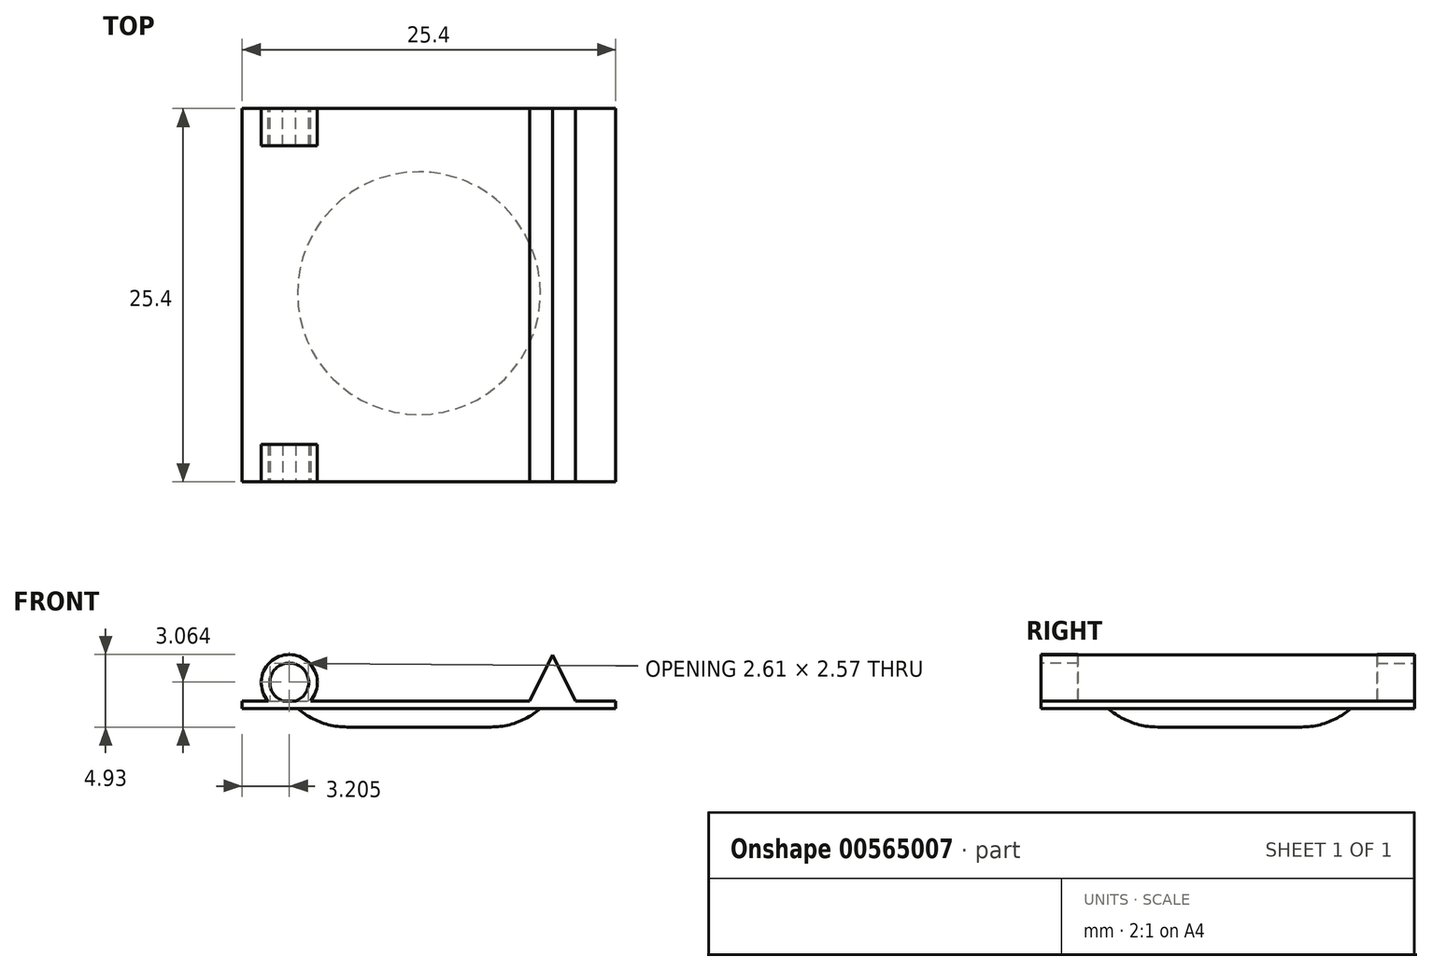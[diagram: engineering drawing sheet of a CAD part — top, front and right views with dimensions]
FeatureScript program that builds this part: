
annotation { "Feature Type Name" : "Feature", "Feature Type Description" : "" }
export const myFeature = defineFeature(function(context is Context, id is Id, definition is map)
    precondition{}
    {
        {
            var Q0;
            Q0=qCreatedBy(makeId("Front.planeOp"),FACE);
            var sketch = newSketch(context, id + "F0", { "sketchPlane" : qUnion([Q0])});
            skLineSegment(sketch, "E0.bottom", {"start": v(-14.15, 0.77) * mm, "end": v(11.25, 0.77) * mm});
            skLineSegment(sketch, "E0.top", {"start": v(-14.15, 0.26) * mm, "end": v(11.25, 0.26) * mm});
            skLineSegment(sketch, "E0.left", {"start": v(-14.15, 0.77) * mm, "end": v(-14.15, 0.26) * mm});
            skLineSegment(sketch, "E0.right", {"start": v(11.25, 0.77) * mm, "end": v(11.25, 0.26) * mm});
            skLineSegment(sketch, "E1", {"start": v(8.52, 0.77) * mm, "end": v(6.95, 3.91) * mm});
            skLineSegment(sketch, "E2", {"start": v(6.95, 3.91) * mm, "end": v(5.4, 0.77) * mm});
            skSolve(sketch);
        }
        {
            var Q0;
            Q0 = qSketchRegion(id + "F0", true);
            extrude(context, id + "F1", {"entities" : qUnion([Q0]), "depth" : 12.7 * mm, "offsetDistance" : 25.4 * mm, "hasSecondDirection" : true, "secondDirectionOppositeDirection" : true, "secondDirectionDepth" : 12.7 * mm});
        }
        {
            var Q0;
            Q0=makeQuery(id+"F1.opExtrude","CAP_FACE",FACE,{"disambiguationData":[OSD([sQuery(id+"F0.wireOp",EDGE,"E0.bottom"),sQuery(id+"F0.wireOp",EDGE,"E0.top"),sQuery(id+"F0.wireOp",EDGE,"E0.left"),sQuery(id+"F0.wireOp",EDGE,"E0.right"),sQuery(id+"F0.wireOp",EDGE,"E1"),sQuery(id+"F0.wireOp",EDGE,"E2")])],"isStart":false});
            var sketch = newSketch(context, id + "F2", { "sketchPlane" : qUnion([Q0])});
            skArc(sketch, "E3", {"start": v(-9.5, 0.77) * mm, "mid": v(-10.95, 3.92) * mm, "end": v(-12.39, 0.77) * mm});
            skArc(sketch, "E4", {"start": v(-10.5, 0.77) * mm, "mid": v(-10.95, 3.34) * mm, "end": v(-11.4, 0.77) * mm});
            skSolve(sketch);
        }
        {
            var Q0;
            {var subQ0=sQuery(id+"F2.wireOp",EDGE,"E3");Q0=makeQuery(id+"F2.imprint","IMPRINT",FACE,{"disambiguationData":[TD([[makeQuery(id+"F2.imprint","IMPRINT",EDGE,{"derivedFrom":subQ0}),1.0]])]});}
            extrude(context, id + "F3", {"entities" : qUnion([Q0]), "operationType" : NewBodyOperationType.ADD, "depth" : 0 * mm, "offsetDistance" : 25.4 * mm, "hasSecondDirection" : true, "secondDirectionOppositeDirection" : true, "secondDirectionDepth" : 2.54 * mm});
        }
        {
            var Q0;
            Q0=makeQuery(id+"F1.opExtrude","SWEPT_BODY",BODY,{"disambiguationData":[OSD([sQuery(id+"F0.wireOp",EDGE,"E0.bottom"),sQuery(id+"F0.wireOp",EDGE,"E0.top"),sQuery(id+"F0.wireOp",EDGE,"E0.left"),sQuery(id+"F0.wireOp",EDGE,"E0.right"),sQuery(id+"F0.wireOp",EDGE,"E1"),sQuery(id+"F0.wireOp",EDGE,"E2")])]});
            var Q1;
            Q1=qCreatedBy(makeId("Front.planeOp"),FACE);
            mirror(context, id + "F4", {"operationType" : NewBodyOperationType.ADD, "entities" : qUnion([Q0]), "mirrorPlane" : qUnion([Q1])});
        }
        {
            var Q0;
            Q0=makeQuery(id+"F1.opExtrude","SWEPT_FACE",FACE,{"disambiguationData":[OSD([sQuery(id+"F0.wireOp",EDGE,"E0.top")])]});
            var sketch = newSketch(context, id + "F5", { "sketchPlane" : qUnion([Q0])});
            skCircle(sketch, "E5", {"center": v(-2.13, -0.13) * mm, "radius": 8.26 * mm});
            skSolve(sketch);
        }
        {
            var Q0;
            Q0 = qSketchRegion(id + "F5", true);
            extrude(context, id + "F6", {"entities" : qUnion([Q0]), "operationType" : NewBodyOperationType.ADD, "depth" : 1.27 * mm, "offsetDistance" : 25.4 * mm});
        }
        {
            var Q0;
            Q0=makeQuery(id+"F6.opExtrude","CAP_EDGE",EDGE,{"disambiguationData":[OSD([sQuery(id+"F5.wireOp",EDGE,"E5")])],"isStart":false});
            fillet(context, id + "F7", {"entities" : qUnion([Q0]), "radius" : 5.08 * mm, "tangentPropagation" : true, "allowEdgeOverflow" : false});
        }
    });
